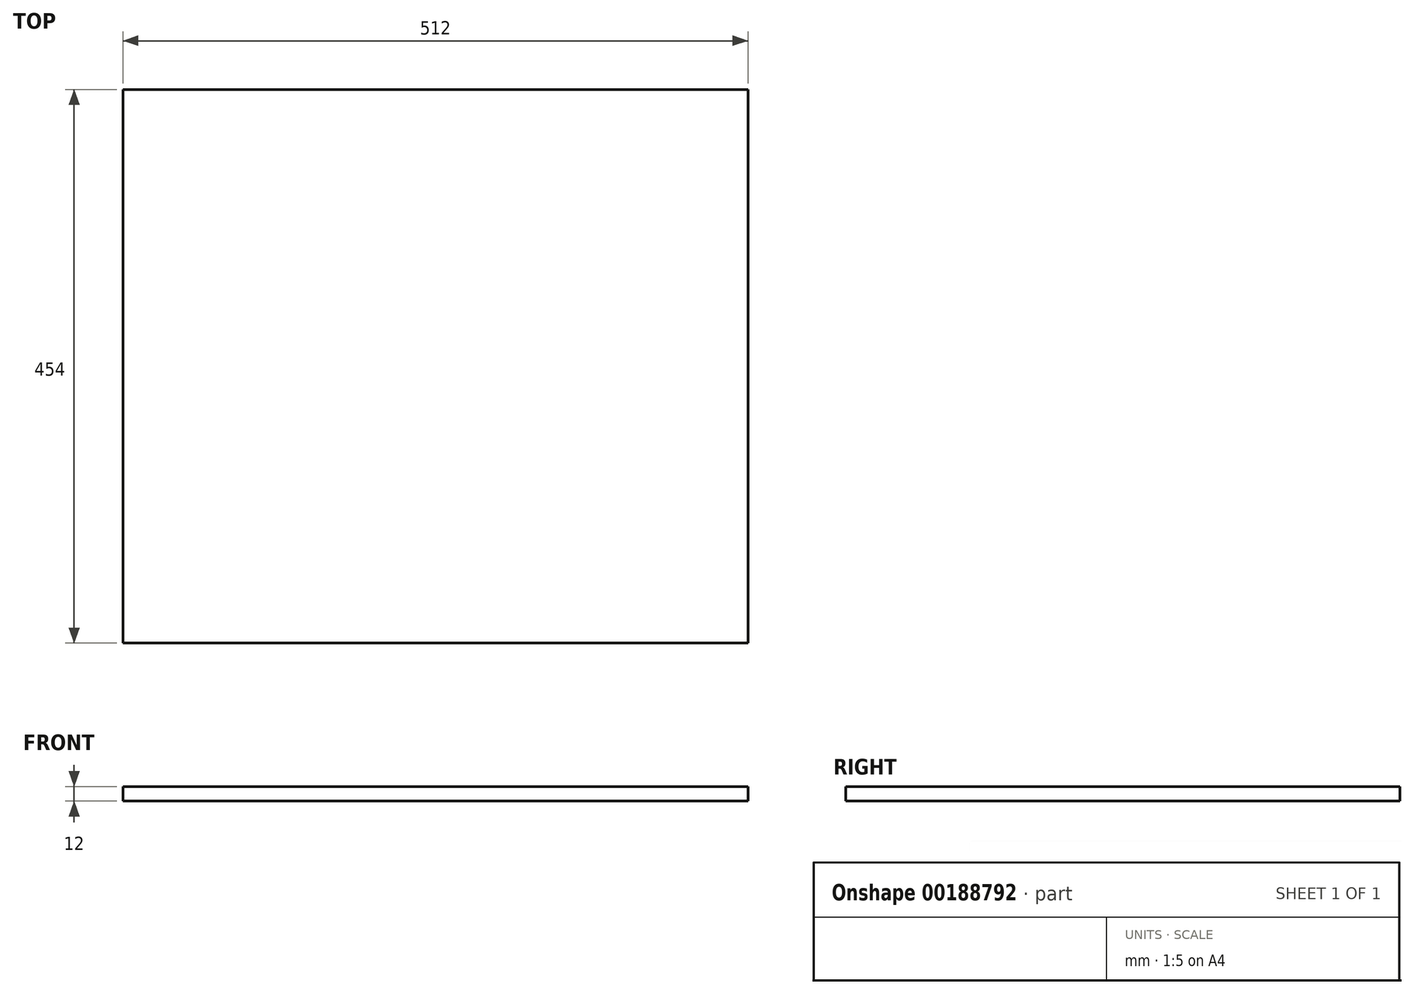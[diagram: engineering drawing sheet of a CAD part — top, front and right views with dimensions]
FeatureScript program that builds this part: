
annotation { "Feature Type Name" : "Feature", "Feature Type Description" : "" }
export const myFeature = defineFeature(function(context is Context, id is Id, definition is map)
    precondition{}
    {
        {
            assignVariable(context, id + "F0", {"name" : "thickness", "anyValue" : 12});
        }
        {
            var Q0;
            Q0=qCreatedBy(makeId("Top.planeOp"),FACE);
            var sketch = newSketch(context, id + "F1", { "sketchPlane" : qUnion([Q0])});
            skLineSegment(sketch, "E0.bottom", {"start": v(256, -227) * mm, "end": v(-256, -227) * mm});
            skLineSegment(sketch, "E0.top", {"start": v(256, 227) * mm, "end": v(-256, 227) * mm});
            skLineSegment(sketch, "E0.left", {"start": v(256, -227) * mm, "end": v(256, 227) * mm});
            skLineSegment(sketch, "E0.right", {"start": v(-256, -227) * mm, "end": v(-256, 227) * mm});
            skPoint(sketch, "E0.middle", {"position": v(0, 0) * mm});
            skSolve(sketch);
        }
        {
            var Q0;
            Q0 = qSketchRegion(id + "F1", true);
            extrude(context, id + "F2", {"entities" : qUnion([Q0]), "depth" : (getVariable(context, 'thickness')) * mm});
        }
    });
